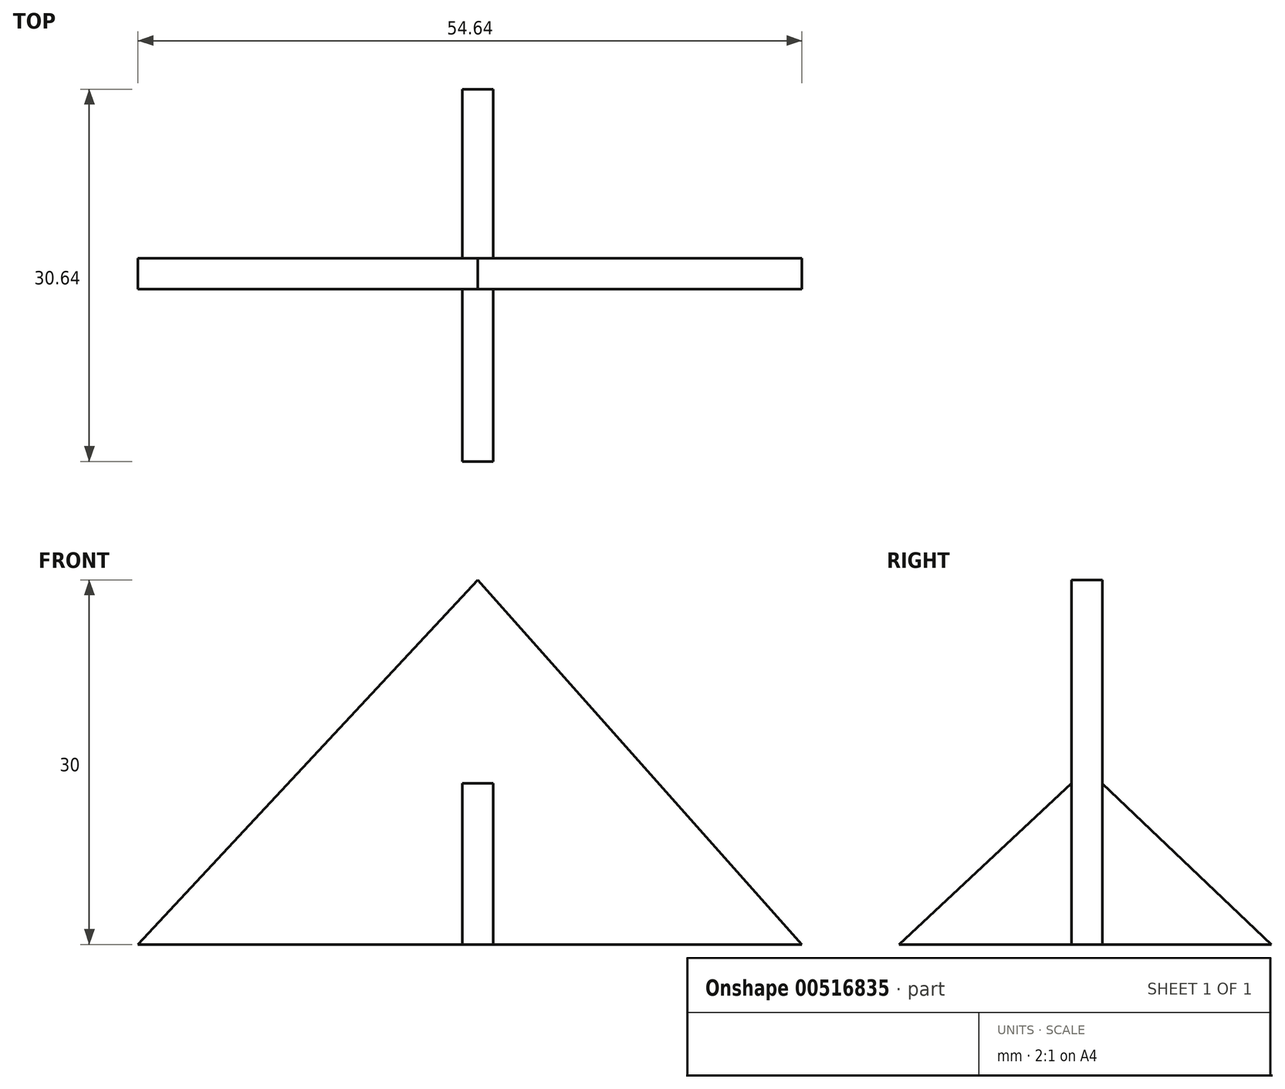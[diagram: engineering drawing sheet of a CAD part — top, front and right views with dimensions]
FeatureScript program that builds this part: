
annotation { "Feature Type Name" : "Feature", "Feature Type Description" : "" }
export const myFeature = defineFeature(function(context is Context, id is Id, definition is map)
    precondition{}
    {
        {
            var Q0;
            Q0=qCreatedBy(makeId("Front.planeOp"),FACE);
            var sketch = newSketch(context, id + "F0", { "sketchPlane" : qUnion([Q0])});
            skLineSegment(sketch, "E0", {"start": v(26.7, 0) * mm, "end": v(-27.95, 0) * mm});
            skLineSegment(sketch, "E1", {"start": v(0, 0) * mm, "end": v(0, 30) * mm});
            skLineSegment(sketch, "E2", {"start": v(0, 30) * mm, "end": v(26.7, 0) * mm});
            skLineSegment(sketch, "E3", {"start": v(0, 30) * mm, "end": v(-27.95, 0) * mm});
            skSolve(sketch);
        }
        {
            var Q0;
            {var subQ2=sQuery(id+"F0.wireOp",EDGE,"E1");Q0=makeQuery(id+"F0.imprint","IMPRINT",FACE,{"disambiguationData":[TD([[makeQuery(id+"F0.imprint","IMPRINT",EDGE,{"derivedFrom":subQ2}),1.0]])]});}
            var Q1;
            {var subQ2=sQuery(id+"F0.wireOp",EDGE,"E1");Q1=makeQuery(id+"F0.imprint","IMPRINT",FACE,{"disambiguationData":[TD([[makeQuery(id+"F0.imprint","IMPRINT",EDGE,{"derivedFrom":subQ2}),-1.0]])]});}
            extrude(context, id + "F1", {"entities" : qUnion([Q0, Q1]), "endBound" : BoundingType.SYMMETRIC, "depth" : 2.54 * mm, "offsetDistance" : 25.4 * mm});
        }
        {
            var Q0;
            Q0=qCreatedBy(makeId("Right.planeOp"),FACE);
            var sketch = newSketch(context, id + "F2", { "sketchPlane" : qUnion([Q0])});
            skLineSegment(sketch, "E4", {"start": v(0, 14.44) * mm, "end": v(15.18, 0) * mm});
            skLineSegment(sketch, "E5", {"start": v(0, 14.44) * mm, "end": v(-15.46, 0) * mm});
            skLineSegment(sketch, "E6", {"start": v(-15.46, 0) * mm, "end": v(15.18, 0) * mm});
            skSolve(sketch);
        }
        {
            var Q0;
            Q0=makeQuery(id+"F2.imprint","IMPRINT",FACE,{"disambiguationData":[TD([[makeQuery(id+"F2.imprint","IMPRINT",EDGE,{"derivedFrom":sQuery(id+"F2.wireOp",EDGE,"E4")}),-1.0]])]});
            extrude(context, id + "F3", {"entities" : qUnion([Q0]), "operationType" : NewBodyOperationType.ADD, "endBound" : BoundingType.SYMMETRIC, "depth" : 2.54 * mm, "offsetDistance" : 25.4 * mm});
        }
    });
